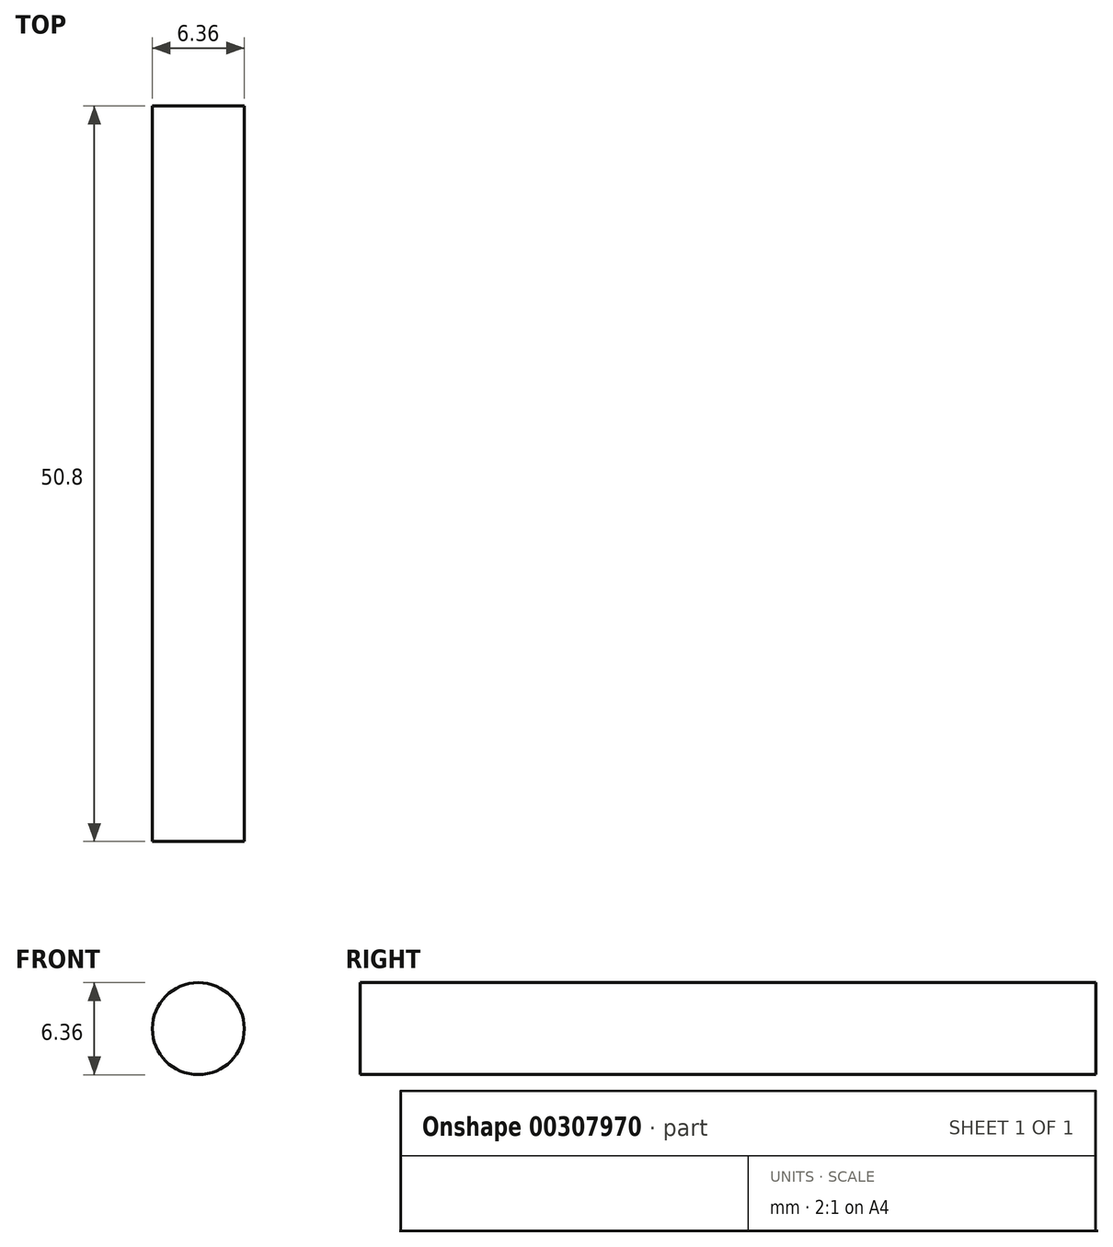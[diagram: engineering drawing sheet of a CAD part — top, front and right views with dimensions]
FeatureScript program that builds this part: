
annotation { "Feature Type Name" : "Feature", "Feature Type Description" : "" }
export const myFeature = defineFeature(function(context is Context, id is Id, definition is map)
    precondition{}
    {
        {
            var Q0;
            Q0=qCreatedBy(makeId("Front.planeOp"),FACE);
            var sketch = newSketch(context, id + "F0", { "sketchPlane" : qUnion([Q0])});
            skCircle(sketch, "E0", {"center": v(0, 0) * mm, "radius": 3.18 * mm});
            skSolve(sketch);
        }
        {
            var Q0;
            Q0=makeQuery(id+"F0.imprint","IMPRINT",FACE,{"disambiguationData":[TD([[makeQuery(id+"F0.imprint","IMPRINT",EDGE,{"derivedFrom":sQuery(id+"F0.wireOp",EDGE,"c3B6SvzG-tsM5-cQ5S-Ywt5-2eVG8OCr4xdT")}),1.0]])]});
            var Q1;
            Q1=makeQuery(id+"F0.imprint","IMPRINT",FACE,{"disambiguationData":[TD([[makeQuery(id+"F0.imprint","IMPRINT",EDGE,{"derivedFrom":sQuery(id+"F0.wireOp",EDGE,"E0")}),1.0]])]});
            extrude(context, id + "F1", {"entities" : qUnion([Q0, Q1]), "depth" : 50.8 * mm});
        }
    });
